# Revit family: Bottle Filling Station_Single Water Fountain_Stainless-VRCDMWSK & LVRCDMWSK
name_source: partatom
category: Plumbing Fixtures
units: mm (PartAtom-declared; Revit-internal decimal feet)

## family parameters
Cut with Voids When Loaded = No
Host = Face
Maintain Annotation Orientation = No
OmniClass Number = 23.65.70.14
OmniClass Title = Fountains
Part Type = Normal
Room Calculation Point = No
Round Connector Dimension = Use Diameter
Shared = No

## types (2) — shared parameters
Default Elevation = 48 "
Height = 456.813 "
Inlet Connection = 0.375 "
Length = 216 "
Main Material = Elkay-Stainless Steel
Manufacturer = Elkay
Manufacturer Brand = Elkay
Outlet Connection = 1.25 "
Product Documentation Link = https://www.elkayfiles.com
Product Installation Sheet URL = https://www.elkayfiles.com
Product Page URL = https://www.elkay.com
URL = https://www.elkay.com
Width = 216.625 "

## per-type parameters (varying)
| type | Description |
| VRCDMWSK | Elkay ezH2O® Vandal-Resistant Bottle Filling Station & Single Fountain Filtered Non-Refrigerated Stainless |
| LVRCDMWSK | Elkay ezH2O® Vandal-Resistant Mechanical Bottle Filling Station & Single Water Fountain Non-Filtered Non-Refrigerated Stainless |

note: column(s) folded — value = type name in every type: Model

## geometry (parser evidence)
native form markers: Sweep x20
no freeform markers — native parametric forms only
